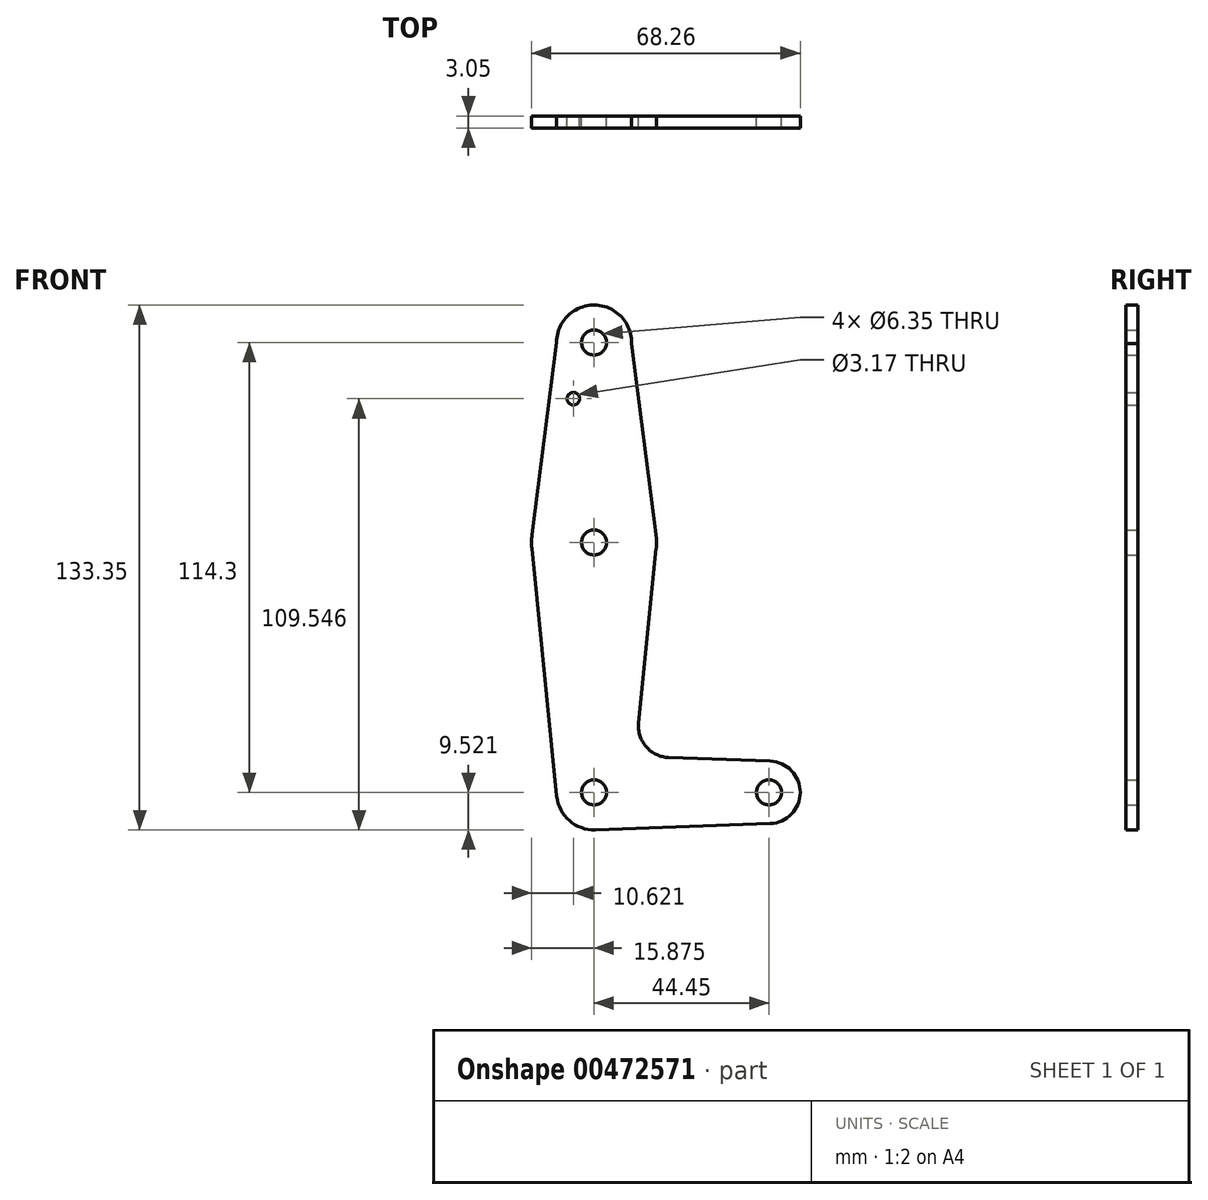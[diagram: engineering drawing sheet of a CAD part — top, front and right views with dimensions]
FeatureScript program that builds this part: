
annotation { "Feature Type Name" : "Feature", "Feature Type Description" : "" }
export const myFeature = defineFeature(function(context is Context, id is Id, definition is map)
    precondition{}
    {
        {
            var Q0;
            Q0=qCreatedBy(makeId("Front.planeOp"),FACE);
            var sketch = newSketch(context, id + "F0", { "sketchPlane" : qUnion([Q0])});
            skLineSegment(sketch, "E0", {"start": v(-10.62, 72.82) * mm, "end": v(-10.62, -41.48) * mm, "construction": true});
            skLineSegment(sketch, "E1", {"start": v(-10.62, -41.48) * mm, "end": v(33.83, -41.48) * mm, "construction": true});
            skCircle(sketch, "E2", {"center": v(-10.62, 72.82) * mm, "radius": 9.53 * mm});
            skCircle(sketch, "E3", {"center": v(-10.62, 22.02) * mm, "radius": 15.88 * mm});
            skCircle(sketch, "E4", {"center": v(-10.62, -41.48) * mm, "radius": 9.53 * mm});
            skCircle(sketch, "E5", {"center": v(33.83, -41.48) * mm, "radius": 7.94 * mm});
            skLineSegment(sketch, "E6", {"start": v(-10.62, 22.02) * mm, "end": v(-10.62, -41.48) * mm});
            skLineSegment(sketch, "E7", {"start": v(-20.14, 72.86) * mm, "end": v(-26.41, 23.65) * mm});
            skLineSegment(sketch, "E8", {"start": v(-1.1, 72.52) * mm, "end": v(5.13, 24.04) * mm});
            skLineSegment(sketch, "E9", {"start": v(8.35, -32.63) * mm, "end": v(34.12, -33.55) * mm});
            skLineSegment(sketch, "E10", {"start": v(34.12, -49.41) * mm, "end": v(-10.62, -51.01) * mm});
            skLineSegment(sketch, "E11", {"start": v(0.73, -23.89) * mm, "end": v(5.18, 20.43) * mm});
            skCircle(sketch, "E12", {"center": v(-10.62, 72.82) * mm, "radius": 3.18 * mm});
            skCircle(sketch, "E13", {"center": v(-10.62, 22.02) * mm, "radius": 3.18 * mm});
            skCircle(sketch, "E14", {"center": v(-10.62, -41.48) * mm, "radius": 3.18 * mm});
            skCircle(sketch, "E15", {"center": v(33.83, -41.48) * mm, "radius": 3.18 * mm});
            skPoint(sketch, "E16.newPointB", {"position": v(-10.62, -31.95) * mm});
            skArc(sketch, "E16.filletArc", {"start": v(0.73, -23.89) * mm, "mid": v(2.65, -29.91) * mm, "end": v(8.35, -32.63) * mm});
            skCircle(sketch, "E17", {"center": v(-15.87, 58.55) * mm, "radius": 1.59 * mm});
            skLineSegment(sketch, "E18", {"start": v(-26.41, 20.43) * mm, "end": v(-20.1, -42.43) * mm});
            skSolve(sketch);
        }
        {
            var Q0;
            Q0 = qSketchRegion(id + "F0", true);
            extrude(context, id + "F1", {"entities" : qUnion([Q0]), "depth" : 3.05 * mm});
        }
    });
